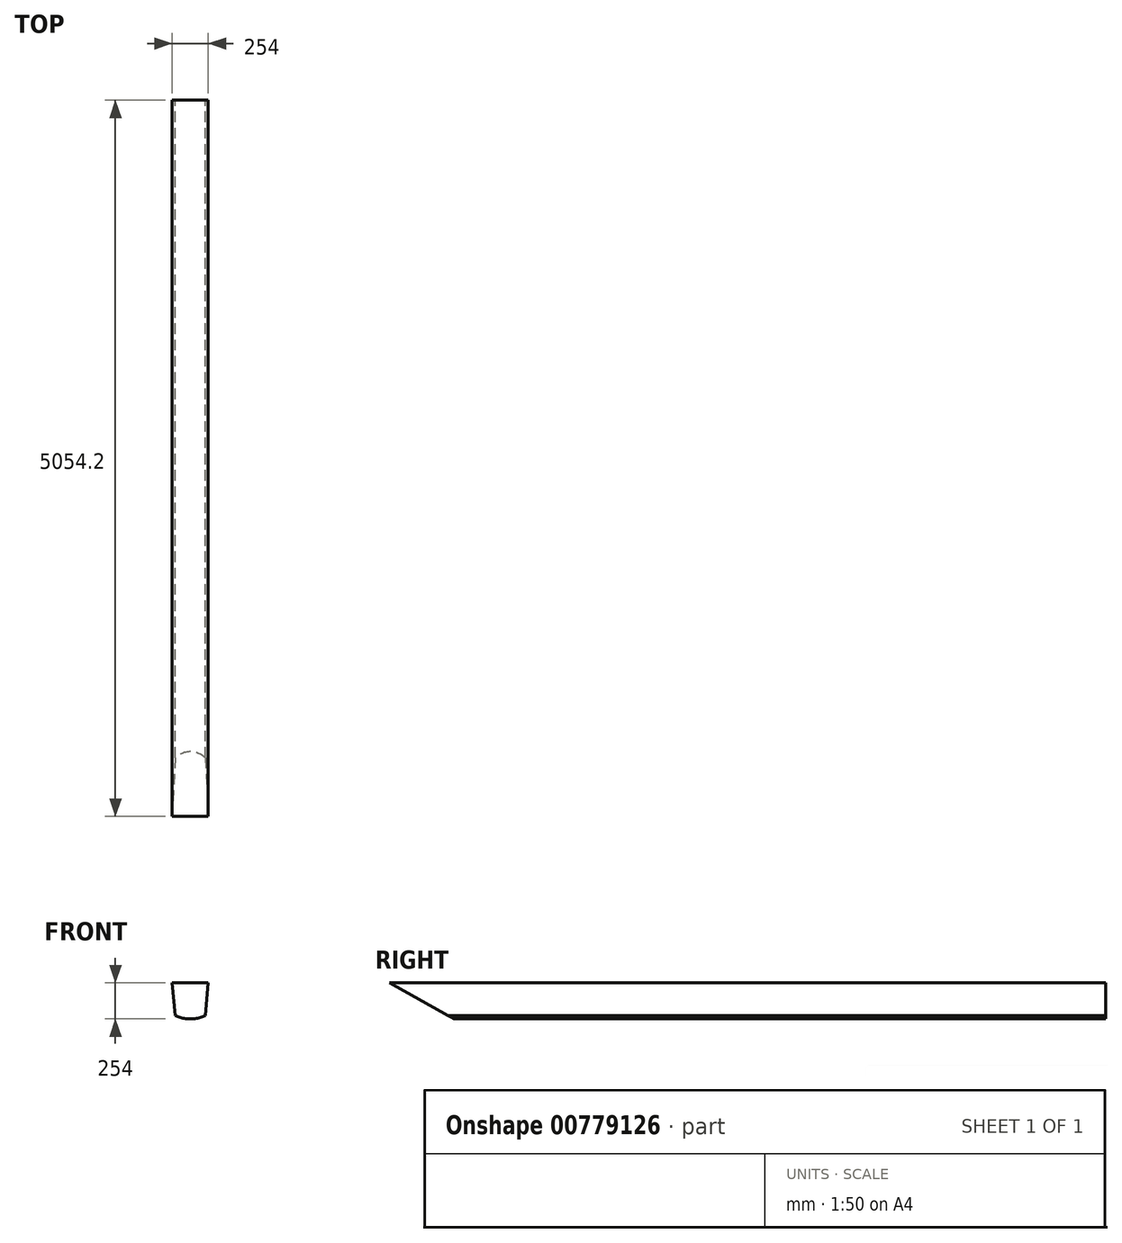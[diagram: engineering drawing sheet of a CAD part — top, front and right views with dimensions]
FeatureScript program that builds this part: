
annotation { "Feature Type Name" : "Feature", "Feature Type Description" : "" }
export const myFeature = defineFeature(function(context is Context, id is Id, definition is map)
    precondition{}
    {
        {
            var Q0;
            Q0=qCreatedBy(makeId("Front.planeOp"),FACE);
            var sketch = newSketch(context, id + "F0", { "sketchPlane" : qUnion([Q0])});
            skArc(sketch, "E0", {"start": v(-106.84, -230.44) * mm, "mid": v(0, -254) * mm, "end": v(106.84, -230.44) * mm});
            skLineSegment(sketch, "E1.bottom", {"start": v(-127, 0) * mm, "end": v(127, 0) * mm});
            skLineSegment(sketch, "E1.left", {"start": v(-127, 0) * mm, "end": v(-106.84, -230.44) * mm});
            skLineSegment(sketch, "E1.right", {"start": v(127, 0) * mm, "end": v(106.84, -230.44) * mm});
            skSolve(sketch);
        }
        {
            var Q0;
            Q0=makeQuery(id+"F0.imprint","IMPRINT",FACE,{"disambiguationData":[TD([[makeQuery(id+"F0.imprint","IMPRINT",EDGE,{"derivedFrom":sQuery(id+"F0.wireOp",EDGE,"E0")}),1.0]])]});
            extrude(context, id + "F1", {"entities" : qUnion([Q0]), "endBound" : BoundingType.SYMMETRIC, "depth" : 5080 * mm, "offsetDistance" : 25.4 * mm});
        }
        {
            var Q0;
            Q0=qCreatedBy(makeId("Right.planeOp"),FACE);
            var sketch = newSketch(context, id + "F2", { "sketchPlane" : qUnion([Q0])});
            skLineSegment(sketch, "E2", {"start": v(-2584.46, 39.06) * mm, "end": v(-1970.97, -301.94) * mm});
            skLineSegment(sketch, "E3", {"start": v(-1970.97, -301.94) * mm, "end": v(-2584.46, -301.94) * mm});
            skLineSegment(sketch, "E4", {"start": v(-2584.46, -301.94) * mm, "end": v(-2584.46, 39.06) * mm});
            skSolve(sketch);
        }
        {
            var Q0;
            Q0=makeQuery(id+"F2.imprint","IMPRINT",FACE,{"disambiguationData":[TD([[makeQuery(id+"F2.imprint","IMPRINT",EDGE,{"derivedFrom":sQuery(id+"F2.wireOp",EDGE,"E2")}),-1.0]])]});
            extrude(context, id + "F3", {"entities" : qUnion([Q0]), "operationType" : NewBodyOperationType.REMOVE, "endBound" : BoundingType.THROUGH_ALL, "depth" : 25.4 * mm, "offsetDistance" : 25.4 * mm, "hasSecondDirection" : true, "secondDirectionBound" : SecondDirectionBoundingType.THROUGH_ALL, "secondDirectionOppositeDirection" : true, "secondDirectionDepth" : 25.4 * mm});
        }
    });
